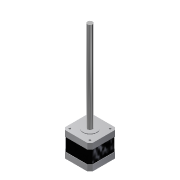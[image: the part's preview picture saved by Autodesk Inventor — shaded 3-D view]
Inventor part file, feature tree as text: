
AUTODESK INVENTOR PART (.ipt)
format: ipt  version: 2014 (Build 180170000, 170)  size: 165,376 bytes
history: native  units: mm
features: extrude x5, sketch x5, chamfer x1, projected_geometry x1
ambient origin geometry x8: Origin, YZ Plane, XZ Plane, XY Plane, X Axis, Y Axis, Z Axis, Center Point
bodies: Solid1 (feature_tree)
feature tree (12):
  extrude  "Extrusion1"  Depth=42.3mm
  chamfer  "Chamfer1"  Distance=9.0mm
  extrude  "Extrusion2"  Depth=0.5mm
  extrude  "Extrusion3"  Depth=0.5mm
  extrude  "Extrusion4"  Depth=20.0mm TaperAngle=0.0deg
  extrude  "Extrusion5"  Depth=9.0mm TaperAngle=0.0deg
  sketch  "Sketch1"  dims[d0=42.3mm d1=31.0mm]
  sketch  "Sketch3"  dims[d2=3.0mm d3=9.0mm d4=0.0mm]
  projected_geometry  "Projected Loop1"
  sketch  "Sketch4"  dims[d5=4.0mm d6=2.0mm d7=45.0deg d8=0.5mm]
  sketch  "Sketch5"  dims[d10=0.5mm d11=0.5mm]
  sketch  "Sketch6"  dims[d12=0.5mm d13=20.0mm d14=0.0mm d15=9.0mm d16=0.0mm d17=22.0mm d18=1.0mm d19=0.0mm d20=8.0mm d21=140.0mm d22=0.0mm]
